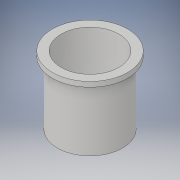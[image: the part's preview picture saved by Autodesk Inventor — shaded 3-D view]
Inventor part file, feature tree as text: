
AUTODESK INVENTOR PART (.ipt)
format: ipt  version: 2017 (Build 210142000, 142)  size: 146,432 bytes
history: native  units: in
note: dims shown in document units (in); Inventor stores cm internally (conversion verified against a paired STEP export)
features: revolve x1, sketch x1
ambient origin geometry x8: Origin, YZ Plane, XZ Plane, XY Plane, X Axis, Y Axis, Z Axis, Center Point
bodies: Body1 (feature_tree)
feature tree (2):
  revolve  "Revolution3"  [1 undecoded]
  sketch  "Sketch1"  dims[d0=1.13in d1=3.75in d2=0.25in d3=0.1718in d5=1.0in d6=1.0in d7=90.0deg d8=0.5in d9=15.0deg d11=0.25in d12=1.25in d13=0.25in d15=0.25in d16=0.5in d17=0.5in d18=0.5in d19=2.5in d20=0.5in d22=0.375in d23=0.25in d25=0.234in d26=15.0deg d29=90.0deg]
note: 1 required parameter value undecoded (feature->parameter linkage not recoverable at this tier; creation-order binding heuristic only, values carry confidence <= 0.55)
